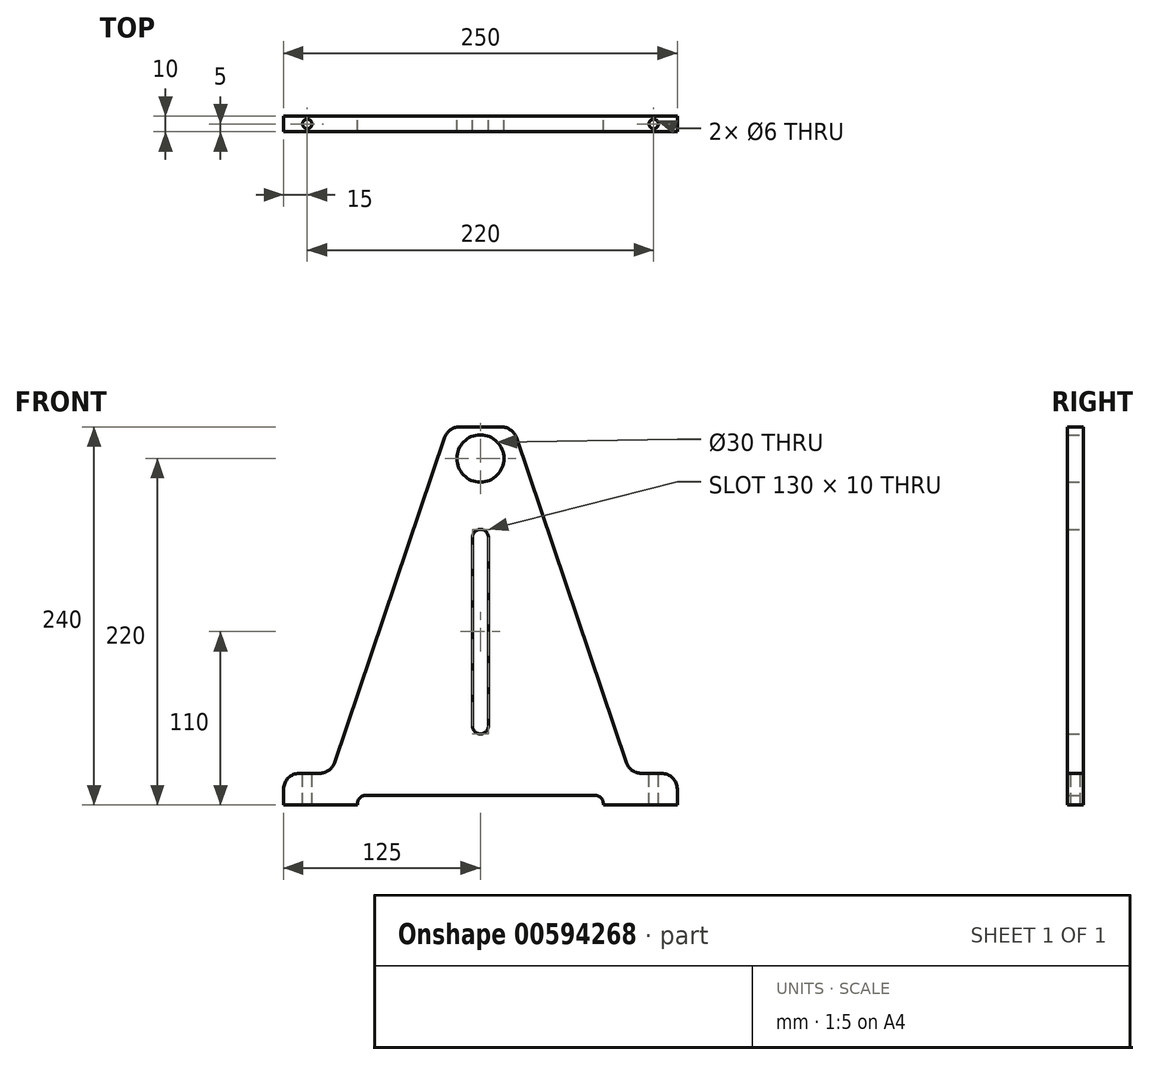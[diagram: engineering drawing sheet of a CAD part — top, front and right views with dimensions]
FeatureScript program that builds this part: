
annotation { "Feature Type Name" : "Feature", "Feature Type Description" : "" }
export const myFeature = defineFeature(function(context is Context, id is Id, definition is map)
    precondition{}
    {
        {
            var Q0;
            Q0=qCreatedBy(makeId("Front.planeOp"),FACE);
            var sketch = newSketch(context, id + "F0", { "sketchPlane" : qUnion([Q0])});
            skLineSegment(sketch, "E0", {"start": v(0, 200) * mm, "end": v(-30, 200) * mm, "construction": true});
            skCircle(sketch, "E1", {"center": v(0, 200) * mm, "radius": 15 * mm});
            skLineSegment(sketch, "E2", {"start": v(-125, -20) * mm, "end": v(-125, -10) * mm});
            skLineSegment(sketch, "E3.0", {"start": v(0, 220) * mm, "end": v(-13.35, 220) * mm});
            skLineSegment(sketch, "E4", {"start": v(-115, 0) * mm, "end": v(-102.17, 0) * mm});
            skLineSegment(sketch, "E5", {"start": v(-92.7, 6.8) * mm, "end": v(-22.82, 213.2) * mm});
            skLineSegment(sketch, "E6.MirrorCS", {"start": v(125, -20) * mm, "end": v(125, -10) * mm});
            skLineSegment(sketch, "E7.MirrorCS", {"start": v(115, 0) * mm, "end": v(102.17, 0) * mm});
            skLineSegment(sketch, "E8.MirrorCS", {"start": v(92.7, 6.8) * mm, "end": v(22.82, 213.2) * mm});
            skLineSegment(sketch, "E9.MirrorCS", {"start": v(0, 220) * mm, "end": v(13.35, 220) * mm});
            skPoint(sketch, "E10.orphan", {"position": v(0, -20) * mm});
            skLineSegment(sketch, "E11", {"start": v(0, -20) * mm, "end": v(0, -14) * mm, "construction": true});
            skLineSegment(sketch, "E12.0", {"start": v(-78, -20) * mm, "end": v(-78, -19) * mm});
            skLineSegment(sketch, "E13.MirrorCS", {"start": v(78, -20) * mm, "end": v(78, -19) * mm});
            skLineSegment(sketch, "E14", {"start": v(-125, -20) * mm, "end": v(-78, -20) * mm});
            skLineSegment(sketch, "E15", {"start": v(-73, -14) * mm, "end": v(73, -14) * mm});
            skLineSegment(sketch, "E16", {"start": v(78, -20) * mm, "end": v(125, -20) * mm});
            skPoint(sketch, "E17.visualSharp", {"position": v(-78, -14) * mm});
            skArc(sketch, "E17.filletArc", {"start": v(-73, -14) * mm, "mid": v(-76.54, -15.46) * mm, "end": v(-78, -19) * mm});
            skPoint(sketch, "E18.visualSharp", {"position": v(78, -14) * mm});
            skArc(sketch, "E18.filletArc", {"start": v(78, -19) * mm, "mid": v(76.54, -15.46) * mm, "end": v(73, -14) * mm});
            skArc(sketch, "E19", {"start": v(-5, 30) * mm, "mid": v(0, 25) * mm, "end": v(5, 30) * mm});
            skArc(sketch, "E20", {"start": v(5, 150) * mm, "mid": v(0, 155) * mm, "end": v(-5, 150) * mm});
            skLineSegment(sketch, "E21", {"start": v(-5, 30) * mm, "end": v(-5, 150) * mm});
            skLineSegment(sketch, "E22.MirrorCS", {"start": v(5, 30) * mm, "end": v(5, 150) * mm});
            skPoint(sketch, "E23.visualSharp", {"position": v(-125, 0) * mm});
            skArc(sketch, "E23.filletArc", {"start": v(-115, 0) * mm, "mid": v(-122.07, -2.93) * mm, "end": v(-125, -10) * mm});
            skPoint(sketch, "E24.visualSharp", {"position": v(-95, 0) * mm});
            skArc(sketch, "E24.filletArc", {"start": v(-102.17, 0) * mm, "mid": v(-96.34, 1.87) * mm, "end": v(-92.7, 6.8) * mm});
            skPoint(sketch, "E25.visualSharp", {"position": v(-20.52, 220) * mm});
            skArc(sketch, "E25.filletArc", {"start": v(-13.35, 220) * mm, "mid": v(-19.18, 218.13) * mm, "end": v(-22.82, 213.2) * mm});
            skPoint(sketch, "E26.visualSharp", {"position": v(20.52, 220) * mm});
            skArc(sketch, "E26.filletArc", {"start": v(22.82, 213.2) * mm, "mid": v(19.18, 218.13) * mm, "end": v(13.35, 220) * mm});
            skPoint(sketch, "E27.visualSharp", {"position": v(95, 0) * mm});
            skArc(sketch, "E27.filletArc", {"start": v(92.7, 6.8) * mm, "mid": v(96.34, 1.87) * mm, "end": v(102.17, 0) * mm});
            skPoint(sketch, "E28.visualSharp", {"position": v(125, 0) * mm});
            skArc(sketch, "E28.filletArc", {"start": v(125, -10) * mm, "mid": v(122.07, -2.93) * mm, "end": v(115, 0) * mm});
            skSolve(sketch);
        }
        {
            var Q0;
            Q0=makeQuery(id+"F0.imprint","IMPRINT",FACE,{"disambiguationData":[TD([[makeQuery(id+"F0.imprint","IMPRINT",EDGE,{"derivedFrom":sQuery(id+"F0.wireOp",EDGE,"GKBg8eNu-DpXV-nyPG-h764-nXgnyL6tIR27")}),-1.0]])]});
            var Q1;
            Q1=makeQuery(id+"F0.imprint","IMPRINT",FACE,{"disambiguationData":[TD([[makeQuery(id+"F0.imprint","IMPRINT",EDGE,{"derivedFrom":sQuery(id+"F0.wireOp",EDGE,"E1")}),-1.0]])]});
            extrude(context, id + "F1", {"entities" : qUnion([Q0, Q1]), "depth" : 10 * mm, "offsetDistance" : 25 * mm});
        }
        {
            var Q0;
            Q0=makeQuery(id+"F1.opExtrude","SWEPT_FACE",FACE,{"disambiguationData":[OSD([sQuery(id+"F0.wireOp",EDGE,"E4")])]});
            var sketch = newSketch(context, id + "F2", { "sketchPlane" : qUnion([Q0])});
            skPoint(sketch, "E29", {"position": v(-110, -5) * mm});
            skPoint(sketch, "E29.positionSnap0", {"position": v(-125, -5) * mm});
            skPoint(sketch, "E30", {"position": v(110, -5) * mm});
            skPoint(sketch, "E30.positionSnap0", {"position": v(-95, -5) * mm});
            skSolve(sketch);
        }
        {
            var Q0;
            Q0=sQuery(id+"F2.wireOp",VERTEX,"E29");
            var Q1;
            Q1=sQuery(id+"F2.wireOp",VERTEX,"E30");
            var Q2;
            Q2=makeQuery(id+"F1.opExtrude","SWEPT_BODY",BODY,{"disambiguationData":[OSD([sQuery(id+"F0.wireOp",EDGE,"E1"),sQuery(id+"F0.wireOp",EDGE,"E2"),sQuery(id+"F0.wireOp",EDGE,"E3.0"),sQuery(id+"F0.wireOp",EDGE,"E4"),sQuery(id+"F0.wireOp",EDGE,"E5"),sQuery(id+"F0.wireOp",EDGE,"E6.MirrorCS"),sQuery(id+"F0.wireOp",EDGE,"E7.MirrorCS"),sQuery(id+"F0.wireOp",EDGE,"E8.MirrorCS"),sQuery(id+"F0.wireOp",EDGE,"E9.MirrorCS"),sQuery(id+"F0.wireOp",EDGE,"E12.0"),sQuery(id+"F0.wireOp",EDGE,"E13.MirrorCS"),sQuery(id+"F0.wireOp",EDGE,"E14"),sQuery(id+"F0.wireOp",EDGE,"E15"),sQuery(id+"F0.wireOp",EDGE,"E16"),sQuery(id+"F0.wireOp",EDGE,"E17.filletArc"),sQuery(id+"F0.wireOp",EDGE,"E18.filletArc"),sQuery(id+"F0.wireOp",EDGE,"E19"),sQuery(id+"F0.wireOp",EDGE,"E20"),sQuery(id+"F0.wireOp",EDGE,"E21"),sQuery(id+"F0.wireOp",EDGE,"E22.MirrorCS")])]});
            hole(context, id + "F3", {"style" : HoleStyle.SIMPLE, "endStyle" : HoleEndStyle.THROUGH, "holeDiameter" : 6 * mm, "majorDiameter" : 5 * mm, "isTappedThrough" : true, "tappedDepth" : 12 * mm, "tapClearance" : 3, "locations" : qUnion([Q0, Q1]), "scope" : qUnion([Q2])});
        }
    });
